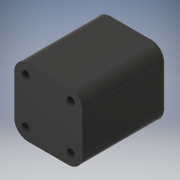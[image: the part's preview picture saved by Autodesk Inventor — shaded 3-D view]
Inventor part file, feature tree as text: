
AUTODESK INVENTOR PART (.ipt)
format: ipt  version: 2019.4 (Build 234330000, 330)  size: 171,520 bytes
history: native  units: mm
features: fillet x3, extrude x2, sketch x1, hole x1
ambient origin geometry x8: Origin, YZ Plane, XZ Plane, XY Plane, X Axis, Y Axis, Z Axis, Center Point
bodies: Solid1 (feature_tree)
feature tree (7):
  sketch  "Sketch1"  dims[d0=20.0mm d1=20.0mm d2=30.0mm d3=30.0mm d4=37.0mm d5=0.0mm d6=26.0mm d7=0.0mm d8=3.5mm d9=6.0mm d10=6.0mm d11=30.0mm d12=90.0deg d13=8.8mm d14=90.0deg d15=6.0mm d16=1.0mm d17=1.0mm]
  extrude  "Extrusion1"  Depth=20.0mm
  extrude  "Extrusion2"  Depth=30.0mm
  hole  "Hole1"  [1 undecoded]
  fillet  "Fillet1"  Radius=37.0mm
  fillet  "Fillet2"  Radius=26.0mm
  fillet  "Fillet3"  Radius=6.0mm
note: 1 required parameter value undecoded (feature->parameter linkage not recoverable at this tier; creation-order binding heuristic only, values carry confidence <= 0.55)
